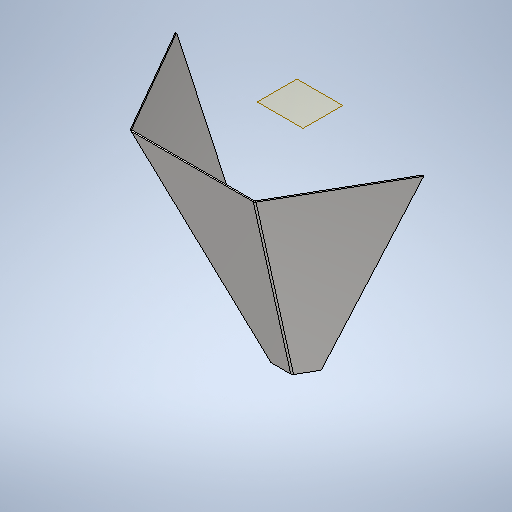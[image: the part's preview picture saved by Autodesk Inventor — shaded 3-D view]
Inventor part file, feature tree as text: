
AUTODESK INVENTOR PART (.ipt)
format: ipt  version: 2025.1 (Build 291241020, 241B)  size: 312,832 bytes
history: native  units: mm
features: sketch x2, other x2, plane x1, loft x1, sheet_metal_op x1
ambient origin geometry x8: Origin, YZ Plane, XZ Plane, XY Plane, X Axis, Y Axis, Z Axis, Center Point
bodies: Body1 (feature_tree)
feature tree (7):
  sketch  "Sketch2"  dims[d5=38.0mm d6=400.0mm]
  plane  "Work Plane1"
  loft  "Lofted Flange1"
  other  "A-Side Definition"
  sketch  "Sketch3"  dims[d7=450.0mm d8=4.0mm d9=4.0mm d16=2.0mm d17=2.0mm d18=2.0mm d19=2.0mm d20=1.0mm d21=4.0mm d22=2.0mm]
  sheet_metal_op  "Bend1"
  other  "Definition1"
